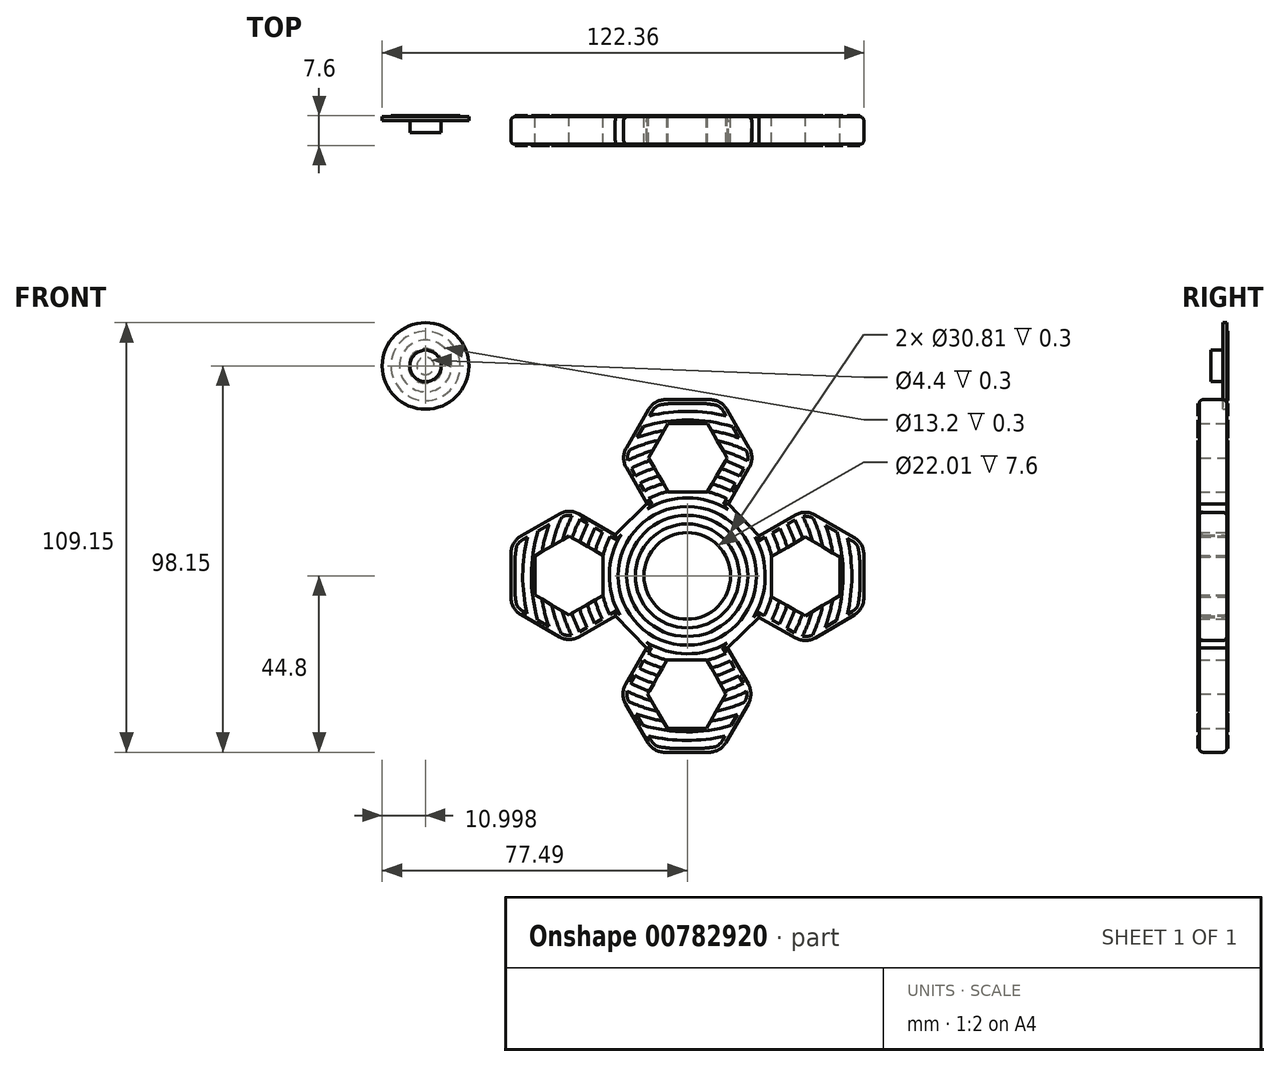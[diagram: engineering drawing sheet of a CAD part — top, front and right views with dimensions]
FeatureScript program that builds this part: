
annotation { "Feature Type Name" : "Feature", "Feature Type Description" : "" }
export const myFeature = defineFeature(function(context is Context, id is Id, definition is map)
    precondition{}
    {
        {
            var Q0;
            Q0=qCreatedBy(makeId("Front.planeOp"),FACE);
            var sketch = newSketch(context, id + "F0", { "sketchPlane" : qUnion([Q0])});
            skCircle(sketch, "E0", {"center": v(0, 0) * mm, "radius": 11 * mm});
            skLineSegment(sketch, "E1.0", {"start": v(-21.35, 5.15) * mm, "end": v(-21.35, -4.88) * mm});
            skLineSegment(sketch, "E1.1", {"start": v(-21.35, -4.88) * mm, "end": v(-30.01, -9.88) * mm});
            skLineSegment(sketch, "E1.2", {"start": v(-30.01, -9.88) * mm, "end": v(-38.67, -4.88) * mm});
            skLineSegment(sketch, "E1.3", {"start": v(-38.67, -4.88) * mm, "end": v(-38.67, 5.12) * mm});
            skLineSegment(sketch, "E1.4", {"start": v(-38.67, 5.12) * mm, "end": v(-30.01, 10.12) * mm});
            skLineSegment(sketch, "E1.5", {"start": v(-30.01, 10.12) * mm, "end": v(-21.35, 5.15) * mm});
            skLineSegment(sketch, "E2.0", {"start": v(10.12, 30.01) * mm, "end": v(5.15, 21.33) * mm});
            skLineSegment(sketch, "E2.1", {"start": v(5.15, 21.33) * mm, "end": v(-4.9, 21.33) * mm});
            skLineSegment(sketch, "E2.2", {"start": v(-4.9, 21.33) * mm, "end": v(-9.89, 30) * mm});
            skLineSegment(sketch, "E2.3", {"start": v(-9.89, 30) * mm, "end": v(-4.88, 38.67) * mm});
            skLineSegment(sketch, "E2.4", {"start": v(-4.88, 38.67) * mm, "end": v(5.12, 38.67) * mm});
            skLineSegment(sketch, "E2.5", {"start": v(5.12, 38.67) * mm, "end": v(10.12, 30.01) * mm});
            skLineSegment(sketch, "E3.0", {"start": v(38.77, -4.96) * mm, "end": v(29.98, -10.14) * mm});
            skLineSegment(sketch, "E3.1", {"start": v(29.98, -10.14) * mm, "end": v(21.45, -5.33) * mm});
            skLineSegment(sketch, "E3.2", {"start": v(21.45, -5.33) * mm, "end": v(21.45, 4.95) * mm});
            skLineSegment(sketch, "E3.3", {"start": v(21.45, 4.95) * mm, "end": v(30, 9.88) * mm});
            skLineSegment(sketch, "E3.4", {"start": v(30, 9.88) * mm, "end": v(38.77, 4.82) * mm});
            skLineSegment(sketch, "E3.5", {"start": v(38.77, 4.82) * mm, "end": v(38.77, -4.96) * mm});
            skLineSegment(sketch, "E4.0", {"start": v(9.88, -30) * mm, "end": v(4.86, -38.7) * mm});
            skLineSegment(sketch, "E4.1", {"start": v(4.86, -38.7) * mm, "end": v(-5.07, -38.7) * mm});
            skLineSegment(sketch, "E4.2", {"start": v(-5.07, -38.7) * mm, "end": v(-10.08, -30.03) * mm});
            skLineSegment(sketch, "E4.3", {"start": v(-10.08, -30.03) * mm, "end": v(-5.1, -21.34) * mm});
            skLineSegment(sketch, "E4.4", {"start": v(-5.1, -21.34) * mm, "end": v(4.9, -21.34) * mm});
            skLineSegment(sketch, "E4.5", {"start": v(4.9, -21.34) * mm, "end": v(9.88, -30) * mm});
            skLineSegment(sketch, "E5.0", {"start": v(-27.52, 15.73) * mm, "end": v(-18.3, 10.44) * mm});
            skLineSegment(sketch, "E5.1", {"start": v(-18.3, -10.17) * mm, "end": v(-27.51, -15.49) * mm});
            skLineSegment(sketch, "E5.2", {"start": v(-32.51, -15.49) * mm, "end": v(-42.28, -9.85) * mm});
            skLineSegment(sketch, "E5.3", {"start": v(-44.78, -5.52) * mm, "end": v(-44.78, 5.76) * mm});
            skLineSegment(sketch, "E5.4", {"start": v(-42.28, 10.09) * mm, "end": v(-32.51, 15.72) * mm});
            skLineSegment(sketch, "E6.0", {"start": v(15.73, 27.52) * mm, "end": v(10.41, 18.25) * mm});
            skLineSegment(sketch, "E6.1", {"start": v(-10.2, 18.34) * mm, "end": v(-15.5, 27.51) * mm});
            skLineSegment(sketch, "E6.2", {"start": v(-15.49, 32.5) * mm, "end": v(-9.85, 42.28) * mm});
            skLineSegment(sketch, "E6.3", {"start": v(-5.52, 44.78) * mm, "end": v(5.76, 44.78) * mm});
            skLineSegment(sketch, "E6.4", {"start": v(10.09, 42.28) * mm, "end": v(15.72, 32.51) * mm});
            skLineSegment(sketch, "E7.0", {"start": v(27.53, -15.77) * mm, "end": v(18.22, -10.51) * mm});
            skLineSegment(sketch, "E7.1", {"start": v(18.27, 10.16) * mm, "end": v(27.5, 15.49) * mm});
            skLineSegment(sketch, "E7.2", {"start": v(32.5, 15.49) * mm, "end": v(42.37, 9.78) * mm});
            skLineSegment(sketch, "E7.3", {"start": v(44.87, 5.45) * mm, "end": v(44.87, -5.59) * mm});
            skLineSegment(sketch, "E7.4", {"start": v(42.41, -9.9) * mm, "end": v(32.53, -15.72) * mm});
            skLineSegment(sketch, "E8.0", {"start": v(-15.69, -27.54) * mm, "end": v(-10.39, -18.3) * mm});
            skLineSegment(sketch, "E8.1", {"start": v(10.21, -18.33) * mm, "end": v(15.49, -27.5) * mm});
            skLineSegment(sketch, "E8.2", {"start": v(15.49, -32.49) * mm, "end": v(9.83, -42.3) * mm});
            skLineSegment(sketch, "E8.3", {"start": v(5.5, -44.8) * mm, "end": v(-5.7, -44.8) * mm});
            skLineSegment(sketch, "E8.4", {"start": v(-10.04, -42.3) * mm, "end": v(-15.68, -32.53) * mm});
            skLineSegment(sketch, "E9", {"start": v(-18.3, -10.17) * mm, "end": v(-10.39, -18.3) * mm});
            skLineSegment(sketch, "E10", {"start": v(10.21, -18.33) * mm, "end": v(18.22, -10.51) * mm});
            skLineSegment(sketch, "E11", {"start": v(18.27, 10.16) * mm, "end": v(10.41, 18.25) * mm});
            skLineSegment(sketch, "E12", {"start": v(-18.3, 10.44) * mm, "end": v(-10.2, 18.34) * mm});
            skPoint(sketch, "E13", {"position": v(-30, 0) * mm});
            skPoint(sketch, "E14", {"position": v(0, 30) * mm});
            skPoint(sketch, "E15", {"position": v(30, 0) * mm});
            skPoint(sketch, "E15.positionSnap0", {"position": v(30, -0.01) * mm});
            skPoint(sketch, "E16", {"position": v(0, -30) * mm});
            skPoint(sketch, "E17.visualSharp", {"position": v(-8.4, 44.78) * mm});
            skArc(sketch, "E17.filletArc", {"start": v(-5.52, 44.78) * mm, "mid": v(-8.02, 44.1) * mm, "end": v(-9.85, 42.28) * mm});
            skPoint(sketch, "E18.visualSharp", {"position": v(8.64, 44.78) * mm});
            skArc(sketch, "E18.filletArc", {"start": v(10.09, 42.28) * mm, "mid": v(8.26, 44.1) * mm, "end": v(5.76, 44.78) * mm});
            skPoint(sketch, "E19.visualSharp", {"position": v(17.16, 30.02) * mm});
            skArc(sketch, "E19.filletArc", {"start": v(15.73, 27.52) * mm, "mid": v(16.4, 30.02) * mm, "end": v(15.72, 32.51) * mm});
            skPoint(sketch, "E20.visualSharp", {"position": v(-16.93, 30.01) * mm});
            skArc(sketch, "E20.filletArc", {"start": v(-15.49, 32.5) * mm, "mid": v(-16.16, 30) * mm, "end": v(-15.5, 27.51) * mm});
            skPoint(sketch, "E21.visualSharp", {"position": v(-30.02, 17.16) * mm});
            skArc(sketch, "E21.filletArc", {"start": v(-27.52, 15.73) * mm, "mid": v(-30.02, 16.4) * mm, "end": v(-32.51, 15.72) * mm});
            skPoint(sketch, "E22.visualSharp", {"position": v(-44.78, 8.64) * mm});
            skArc(sketch, "E22.filletArc", {"start": v(-42.28, 10.09) * mm, "mid": v(-44.1, 8.26) * mm, "end": v(-44.78, 5.76) * mm});
            skPoint(sketch, "E23.visualSharp", {"position": v(-44.78, -8.4) * mm});
            skArc(sketch, "E23.filletArc", {"start": v(-44.78, -5.52) * mm, "mid": v(-44.1, -8.02) * mm, "end": v(-42.28, -9.85) * mm});
            skPoint(sketch, "E24.visualSharp", {"position": v(-30.01, -16.93) * mm});
            skArc(sketch, "E24.filletArc", {"start": v(-32.51, -15.49) * mm, "mid": v(-30.01, -16.16) * mm, "end": v(-27.51, -15.49) * mm});
            skPoint(sketch, "E25.visualSharp", {"position": v(-17.12, -30.04) * mm});
            skArc(sketch, "E25.filletArc", {"start": v(-15.69, -27.54) * mm, "mid": v(-16.35, -30.04) * mm, "end": v(-15.68, -32.53) * mm});
            skPoint(sketch, "E26.visualSharp", {"position": v(-8.6, -44.8) * mm});
            skArc(sketch, "E26.filletArc", {"start": v(-10.04, -42.3) * mm, "mid": v(-8.2, -44.13) * mm, "end": v(-5.7, -44.8) * mm});
            skPoint(sketch, "E27.visualSharp", {"position": v(8.4, -44.8) * mm});
            skArc(sketch, "E27.filletArc", {"start": v(5.5, -44.8) * mm, "mid": v(8, -44.13) * mm, "end": v(9.83, -42.3) * mm});
            skPoint(sketch, "E28.visualSharp", {"position": v(16.93, -30) * mm});
            skArc(sketch, "E28.filletArc", {"start": v(15.49, -32.49) * mm, "mid": v(16.16, -30) * mm, "end": v(15.49, -27.5) * mm});
            skPoint(sketch, "E29.visualSharp", {"position": v(30.04, -17.19) * mm});
            skArc(sketch, "E29.filletArc", {"start": v(27.53, -15.77) * mm, "mid": v(30.04, -16.41) * mm, "end": v(32.53, -15.72) * mm});
            skPoint(sketch, "E30.visualSharp", {"position": v(44.87, -8.44) * mm});
            skArc(sketch, "E30.filletArc", {"start": v(42.41, -9.9) * mm, "mid": v(44.21, -8.07) * mm, "end": v(44.87, -5.59) * mm});
            skPoint(sketch, "E31.visualSharp", {"position": v(44.87, 8.34) * mm});
            skArc(sketch, "E31.filletArc", {"start": v(44.87, 5.45) * mm, "mid": v(44.2, 7.95) * mm, "end": v(42.37, 9.78) * mm});
            skPoint(sketch, "E32.visualSharp", {"position": v(30, 16.93) * mm});
            skArc(sketch, "E32.filletArc", {"start": v(32.5, 15.49) * mm, "mid": v(30, 16.16) * mm, "end": v(27.5, 15.49) * mm});
            skCircle(sketch, "E33", {"center": v(-66.5, 53.35) * mm, "radius": 11 * mm});
            skSolve(sketch);
        }
        {
            var Q0;
            Q0=makeQuery(id+"F0.imprint","IMPRINT",FACE,{"disambiguationData":[TD([[makeQuery(id+"F0.imprint","IMPRINT",EDGE,{"derivedFrom":sQuery(id+"F0.wireOp",EDGE,"E0")}),-1.0]])]});
            extrude(context, id + "F1", {"entities" : qUnion([Q0]), "depth" : 7 * mm, "offsetDistance" : 25 * mm});
        }
        {
            var Q0;
            Q0=makeQuery(id+"F1.opExtrude","CAP_EDGE",EDGE,{"disambiguationData":[OSD([sQuery(id+"F0.wireOp",EDGE,"E8.2")])],"isStart":false});
            var Q1;
            Q1=makeQuery(id+"F1.opExtrude","CAP_EDGE",EDGE,{"disambiguationData":[OSD([sQuery(id+"F0.wireOp",EDGE,"E5.3")])],"isStart":false});
            var Q2;
            Q2=makeQuery(id+"F1.opExtrude","CAP_EDGE",EDGE,{"disambiguationData":[OSD([sQuery(id+"F0.wireOp",EDGE,"E6.2")])],"isStart":false});
            var Q3;
            Q3=makeQuery(id+"F1.opExtrude","CAP_EDGE",EDGE,{"disambiguationData":[OSD([sQuery(id+"F0.wireOp",EDGE,"E7.1")])],"isStart":false});
            var Q4;
            Q4=makeQuery(id+"F1.opExtrude","CAP_EDGE",EDGE,{"disambiguationData":[OSD([sQuery(id+"F0.wireOp",EDGE,"E11")])],"isStart":false});
            var Q5;
            Q5=makeQuery(id+"F1.opExtrude","CAP_EDGE",EDGE,{"disambiguationData":[OSD([sQuery(id+"F0.wireOp",EDGE,"E11")])],"isStart":true});
            var Q6;
            Q6=makeQuery(id+"F1.opExtrude","CAP_EDGE",EDGE,{"disambiguationData":[OSD([sQuery(id+"F0.wireOp",EDGE,"E6.0")])],"isStart":true});
            var Q7;
            Q7=makeQuery(id+"F1.opExtrude","CAP_EDGE",EDGE,{"disambiguationData":[OSD([sQuery(id+"F0.wireOp",EDGE,"E7.2")])],"isStart":true});
            var Q8;
            Q8=makeQuery(id+"F1.opExtrude","CAP_EDGE",EDGE,{"disambiguationData":[OSD([sQuery(id+"F0.wireOp",EDGE,"E12")])],"isStart":true});
            var Q9;
            Q9=makeQuery(id+"F1.opExtrude","CAP_EDGE",EDGE,{"disambiguationData":[OSD([sQuery(id+"F0.wireOp",EDGE,"E5.0")])],"isStart":true});
            var Q10;
            Q10=makeQuery(id+"F1.opExtrude","CAP_EDGE",EDGE,{"disambiguationData":[OSD([sQuery(id+"F0.wireOp",EDGE,"E9")])],"isStart":true});
            var Q11;
            Q11=makeQuery(id+"F1.opExtrude","CAP_EDGE",EDGE,{"disambiguationData":[OSD([sQuery(id+"F0.wireOp",EDGE,"E8.0")])],"isStart":true});
            var Q12;
            Q12=makeQuery(id+"F1.opExtrude","CAP_EDGE",EDGE,{"disambiguationData":[OSD([sQuery(id+"F0.wireOp",EDGE,"E10")])],"isStart":true});
            var Q13;
            Q13=makeQuery(id+"F1.opExtrude","CAP_EDGE",EDGE,{"disambiguationData":[OSD([sQuery(id+"F0.wireOp",EDGE,"E10")])],"isStart":false});
            var Q14;
            Q14=makeQuery(id+"F1.opExtrude","CAP_EDGE",EDGE,{"disambiguationData":[OSD([sQuery(id+"F0.wireOp",EDGE,"E9")])],"isStart":false});
            var Q15;
            Q15=makeQuery(id+"F1.opExtrude","CAP_EDGE",EDGE,{"disambiguationData":[OSD([sQuery(id+"F0.wireOp",EDGE,"E12")])],"isStart":false});
            fillet(context, id + "F2", {"entities" : qUnion([Q0, Q1, Q2, Q3, Q4, Q5, Q6, Q7, Q8, Q9, Q10, Q11, Q12, Q13, Q14, Q15]), "radius" : 1 * mm, "tangentPropagation" : true, "allowEdgeOverflow" : false});
        }
        {
            var Q0;
            Q0=makeQuery(id+"F1.opExtrude","CAP_FACE",FACE,{"disambiguationData":[OSD([sQuery(id+"F0.wireOp",EDGE,"E0"),sQuery(id+"F0.wireOp",EDGE,"E1.0"),sQuery(id+"F0.wireOp",EDGE,"E1.1"),sQuery(id+"F0.wireOp",EDGE,"E1.2"),sQuery(id+"F0.wireOp",EDGE,"E1.3"),sQuery(id+"F0.wireOp",EDGE,"E1.4"),sQuery(id+"F0.wireOp",EDGE,"E1.5"),sQuery(id+"F0.wireOp",EDGE,"E2.0"),sQuery(id+"F0.wireOp",EDGE,"E2.1"),sQuery(id+"F0.wireOp",EDGE,"E2.2"),sQuery(id+"F0.wireOp",EDGE,"E2.3"),sQuery(id+"F0.wireOp",EDGE,"E2.4"),sQuery(id+"F0.wireOp",EDGE,"E2.5"),sQuery(id+"F0.wireOp",EDGE,"E3.0"),sQuery(id+"F0.wireOp",EDGE,"E3.1"),sQuery(id+"F0.wireOp",EDGE,"E3.2"),sQuery(id+"F0.wireOp",EDGE,"E3.3"),sQuery(id+"F0.wireOp",EDGE,"E3.4"),sQuery(id+"F0.wireOp",EDGE,"E3.5"),sQuery(id+"F0.wireOp",EDGE,"E4.0"),sQuery(id+"F0.wireOp",EDGE,"E4.1"),sQuery(id+"F0.wireOp",EDGE,"E4.2"),sQuery(id+"F0.wireOp",EDGE,"E4.3"),sQuery(id+"F0.wireOp",EDGE,"E4.4"),sQuery(id+"F0.wireOp",EDGE,"E4.5"),sQuery(id+"F0.wireOp",EDGE,"E5.0"),sQuery(id+"F0.wireOp",EDGE,"E5.1"),sQuery(id+"F0.wireOp",EDGE,"E5.2"),sQuery(id+"F0.wireOp",EDGE,"E5.3"),sQuery(id+"F0.wireOp",EDGE,"E5.4"),sQuery(id+"F0.wireOp",EDGE,"E6.0"),sQuery(id+"F0.wireOp",EDGE,"E6.1"),sQuery(id+"F0.wireOp",EDGE,"E6.2"),sQuery(id+"F0.wireOp",EDGE,"E6.3"),sQuery(id+"F0.wireOp",EDGE,"E6.4"),sQuery(id+"F0.wireOp",EDGE,"E7.0"),sQuery(id+"F0.wireOp",EDGE,"E7.1"),sQuery(id+"F0.wireOp",EDGE,"E7.2"),sQuery(id+"F0.wireOp",EDGE,"E7.3"),sQuery(id+"F0.wireOp",EDGE,"E7.4"),sQuery(id+"F0.wireOp",EDGE,"E8.0"),sQuery(id+"F0.wireOp",EDGE,"E8.1"),sQuery(id+"F0.wireOp",EDGE,"E8.2"),sQuery(id+"F0.wireOp",EDGE,"E8.3"),sQuery(id+"F0.wireOp",EDGE,"E8.4"),sQuery(id+"F0.wireOp",EDGE,"E9"),sQuery(id+"F0.wireOp",EDGE,"E10"),sQuery(id+"F0.wireOp",EDGE,"E11"),sQuery(id+"F0.wireOp",EDGE,"E12"),sQuery(id+"F0.wireOp",EDGE,"E17.filletArc"),sQuery(id+"F0.wireOp",EDGE,"E18.filletArc"),sQuery(id+"F0.wireOp",EDGE,"E19.filletArc"),sQuery(id+"F0.wireOp",EDGE,"E20.filletArc"),sQuery(id+"F0.wireOp",EDGE,"E21.filletArc"),sQuery(id+"F0.wireOp",EDGE,"E22.filletArc"),sQuery(id+"F0.wireOp",EDGE,"E23.filletArc"),sQuery(id+"F0.wireOp",EDGE,"E24.filletArc"),sQuery(id+"F0.wireOp",EDGE,"E25.filletArc"),sQuery(id+"F0.wireOp",EDGE,"E26.filletArc"),sQuery(id+"F0.wireOp",EDGE,"E27.filletArc"),sQuery(id+"F0.wireOp",EDGE,"E28.filletArc"),sQuery(id+"F0.wireOp",EDGE,"E29.filletArc"),sQuery(id+"F0.wireOp",EDGE,"E30.filletArc"),sQuery(id+"F0.wireOp",EDGE,"E31.filletArc"),sQuery(id+"F0.wireOp",EDGE,"E32.filletArc")])],"isStart":false});
            var sketch = newSketch(context, id + "F3", { "sketchPlane" : qUnion([Q0])});
            skLineSegment(sketch, "E34", {"start": v(0, -2.4) * mm, "end": v(0, -77.28) * mm});
            skLineSegment(sketch, "E35", {"start": v(0, -2.4) * mm, "end": v(0, 53.22) * mm});
            skLineSegment(sketch, "E36", {"start": v(0, 0) * mm, "end": v(-74.78, 0) * mm});
            skLineSegment(sketch, "E37", {"start": v(0, 0) * mm, "end": v(76.06, 0) * mm});
            skCircle(sketch, "E38.0", {"center": v(0, 0) * mm, "radius": 13.2 * mm});
            skCircle(sketch, "E39.0", {"center": v(0, 0) * mm, "radius": 15.4 * mm});
            skCircle(sketch, "E40.0", {"center": v(0, 0) * mm, "radius": 17.6 * mm});
            skCircle(sketch, "E41.0", {"center": v(0, 0) * mm, "radius": 19.8 * mm});
            skCircle(sketch, "E42.0", {"center": v(0, 0) * mm, "radius": 22 * mm});
            skCircle(sketch, "E43.0", {"center": v(0, 0) * mm, "radius": 24.2 * mm});
            skCircle(sketch, "E44.0", {"center": v(0, 0) * mm, "radius": 26.4 * mm});
            skCircle(sketch, "E45.0", {"center": v(0, 0) * mm, "radius": 28.6 * mm});
            skCircle(sketch, "E46.0", {"center": v(0, 0) * mm, "radius": 30.8 * mm});
            skCircle(sketch, "E47.0", {"center": v(0, 0) * mm, "radius": 33 * mm});
            skCircle(sketch, "E48.0", {"center": v(0, 0) * mm, "radius": 35.2 * mm});
            skCircle(sketch, "E49.0", {"center": v(0, 0) * mm, "radius": 37.4 * mm});
            skCircle(sketch, "E50.0", {"center": v(0, 0) * mm, "radius": 39.6 * mm});
            skCircle(sketch, "E51.0", {"center": v(0, 0) * mm, "radius": 41.8 * mm});
            skCircle(sketch, "E52.0", {"center": v(0, 0) * mm, "radius": 44 * mm});
            skSolve(sketch);
        }
        {
            var Q0;
            {var subQ9=sQuery(id+"F3.wireOp",EDGE,"E51.0");var subQ10=sQuery(id+"F3.wireOp",EDGE,"E35");var subQ11=makeQuery(id+"F3.imprint","INTERSECT",VERTEX,{"derivedFrom":[subQ10,subQ9]});Q0=makeQuery(id+"F3.imprint","IMPRINT",FACE,{"disambiguationData":[TD([[makeQuery(id+"F3.imprint","IMPRINT",EDGE,{"disambiguationData":[TD([[subQ11,-1.0]])],"derivedFrom":subQ10}),1.0]])]});}
            var Q1;
            {var subQ7=sQuery(id+"F3.wireOp",EDGE,"E51.0");var subQ13=sQuery(id+"F3.wireOp",EDGE,"E35");var subQ15=makeQuery(id+"F3.imprint","INTERSECT",VERTEX,{"derivedFrom":[subQ13,subQ7]});Q1=makeQuery(id+"F3.imprint","IMPRINT",FACE,{"disambiguationData":[TD([[makeQuery(id+"F3.imprint","IMPRINT",EDGE,{"disambiguationData":[TD([[subQ15,-1.0]])],"derivedFrom":subQ13}),-1.0]])]});}
            var Q2;
            {var subQ10=sQuery(id+"F3.wireOp",EDGE,"E50.0");var subQ11=sQuery(id+"F3.wireOp",EDGE,"E35");var subQ12=makeQuery(id+"F3.imprint","INTERSECT",VERTEX,{"derivedFrom":[subQ11,subQ10]});Q2=makeQuery(id+"F3.imprint","IMPRINT",FACE,{"disambiguationData":[TD([[makeQuery(id+"F3.imprint","IMPRINT",EDGE,{"disambiguationData":[TD([[subQ12,1.0]])],"derivedFrom":subQ11}),1.0]])]});}
            var Q3;
            {var subQ5=sQuery(id+"F3.wireOp",EDGE,"E35");var subQ7=sQuery(id+"F3.wireOp",EDGE,"E50.0");var subQ8=makeQuery(id+"F3.imprint","INTERSECT",VERTEX,{"derivedFrom":[subQ5,subQ7]});Q3=makeQuery(id+"F3.imprint","IMPRINT",FACE,{"disambiguationData":[TD([[makeQuery(id+"F3.imprint","IMPRINT",EDGE,{"disambiguationData":[TD([[subQ8,1.0]])],"derivedFrom":subQ5}),-1.0]])]});}
            var Q4;
            {var subQ2=sQuery(id+"F0.wireOp",EDGE,"E2.3");var subQ7=sQuery(id+"F3.wireOp",EDGE,"E47.0");var subQ11=makeQuery(id+"F1.opExtrude","CAP_EDGE",EDGE,{"disambiguationData":[OSD([subQ2])],"isStart":false});var subQ13=makeQuery(id+"F3.imprint","INTERSECT",VERTEX,{"derivedFrom":[subQ11,subQ7]});Q4=makeQuery(id+"F3.imprint","IMPRINT",FACE,{"disambiguationData":[TD([[makeQuery(id+"F3.imprint","IMPRINT",EDGE,{"disambiguationData":[TD([[subQ13,-1.0]])],"derivedFrom":subQ11}),1.0]])]});}
            var Q5;
            {var subQ0=sQuery(id+"F3.wireOp",EDGE,"E47.0");var subQ2=sQuery(id+"F0.wireOp",EDGE,"E2.5");var subQ5=makeQuery(id+"F1.opExtrude","CAP_EDGE",EDGE,{"disambiguationData":[OSD([subQ2])],"isStart":false});var subQ6=makeQuery(id+"F3.imprint","INTERSECT",VERTEX,{"derivedFrom":[subQ5,subQ0]});Q5=makeQuery(id+"F3.imprint","IMPRINT",FACE,{"disambiguationData":[TD([[makeQuery(id+"F3.imprint","IMPRINT",EDGE,{"disambiguationData":[TD([[subQ6,1.0]])],"derivedFrom":subQ5}),1.0]])]});}
            var Q6;
            {var subQ0=sQuery(id+"F3.wireOp",EDGE,"E45.0");var subQ1=sQuery(id+"F0.wireOp",EDGE,"E2.2");var subQ2=makeQuery(id+"F1.opExtrude","CAP_EDGE",EDGE,{"disambiguationData":[OSD([subQ1])],"isStart":false});var subQ3=makeQuery(id+"F3.imprint","INTERSECT",VERTEX,{"derivedFrom":[subQ2,subQ0]});Q6=makeQuery(id+"F3.imprint","IMPRINT",FACE,{"disambiguationData":[TD([[makeQuery(id+"F3.imprint","IMPRINT",EDGE,{"disambiguationData":[TD([[subQ3,-1.0]])],"derivedFrom":subQ2}),1.0]])]});}
            var Q7;
            {var subQ0=sQuery(id+"F3.wireOp",EDGE,"E45.0");var subQ2=sQuery(id+"F0.wireOp",EDGE,"E2.0");var subQ5=makeQuery(id+"F1.opExtrude","CAP_EDGE",EDGE,{"disambiguationData":[OSD([subQ2])],"isStart":false});var subQ6=makeQuery(id+"F3.imprint","INTERSECT",VERTEX,{"derivedFrom":[subQ5,subQ0]});Q7=makeQuery(id+"F3.imprint","IMPRINT",FACE,{"disambiguationData":[TD([[makeQuery(id+"F3.imprint","IMPRINT",EDGE,{"disambiguationData":[TD([[subQ6,1.0]])],"derivedFrom":subQ5}),1.0]])]});}
            var Q8;
            {var subQ0=sQuery(id+"F3.wireOp",EDGE,"E43.0");var subQ1=sQuery(id+"F0.wireOp",EDGE,"E2.2");var subQ2=makeQuery(id+"F1.opExtrude","CAP_EDGE",EDGE,{"disambiguationData":[OSD([subQ1])],"isStart":false});var subQ3=makeQuery(id+"F3.imprint","INTERSECT",VERTEX,{"derivedFrom":[subQ2,subQ0]});Q8=makeQuery(id+"F3.imprint","IMPRINT",FACE,{"disambiguationData":[TD([[makeQuery(id+"F3.imprint","IMPRINT",EDGE,{"disambiguationData":[TD([[subQ3,-1.0]])],"derivedFrom":subQ2}),1.0]])]});}
            var Q9;
            {var subQ0=sQuery(id+"F3.wireOp",EDGE,"E43.0");var subQ2=sQuery(id+"F0.wireOp",EDGE,"E2.0");var subQ5=makeQuery(id+"F1.opExtrude","CAP_EDGE",EDGE,{"disambiguationData":[OSD([subQ2])],"isStart":false});var subQ6=makeQuery(id+"F3.imprint","INTERSECT",VERTEX,{"derivedFrom":[subQ5,subQ0]});Q9=makeQuery(id+"F3.imprint","IMPRINT",FACE,{"disambiguationData":[TD([[makeQuery(id+"F3.imprint","IMPRINT",EDGE,{"disambiguationData":[TD([[subQ6,1.0]])],"derivedFrom":subQ5}),1.0]])]});}
            var Q10;
            {var subQ10=sQuery(id+"F3.wireOp",EDGE,"E41.0");var subQ11=sQuery(id+"F3.wireOp",EDGE,"E35");var subQ12=makeQuery(id+"F3.imprint","INTERSECT",VERTEX,{"derivedFrom":[subQ11,subQ10]});Q10=makeQuery(id+"F3.imprint","IMPRINT",FACE,{"disambiguationData":[TD([[makeQuery(id+"F3.imprint","IMPRINT",EDGE,{"disambiguationData":[TD([[subQ12,-1.0]])],"derivedFrom":subQ11}),1.0]])]});}
            var Q11;
            {var subQ12=sQuery(id+"F3.wireOp",EDGE,"E41.0");var subQ13=sQuery(id+"F3.wireOp",EDGE,"E35");var subQ14=makeQuery(id+"F3.imprint","INTERSECT",VERTEX,{"derivedFrom":[subQ13,subQ12]});Q11=makeQuery(id+"F3.imprint","IMPRINT",FACE,{"disambiguationData":[TD([[makeQuery(id+"F3.imprint","IMPRINT",EDGE,{"disambiguationData":[TD([[subQ14,-1.0]])],"derivedFrom":subQ13}),-1.0]])]});}
            var Q12;
            {var subQ0=sQuery(id+"F3.wireOp",EDGE,"E39.0");var subQ1=sQuery(id+"F3.wireOp",EDGE,"E35");var subQ2=makeQuery(id+"F3.imprint","INTERSECT",VERTEX,{"derivedFrom":[subQ1,subQ0]});Q12=makeQuery(id+"F3.imprint","IMPRINT",FACE,{"disambiguationData":[TD([[makeQuery(id+"F3.imprint","IMPRINT",EDGE,{"disambiguationData":[TD([[subQ2,-1.0]])],"derivedFrom":subQ1}),1.0]])]});}
            var Q13;
            {var subQ0=sQuery(id+"F3.wireOp",EDGE,"E39.0");var subQ1=sQuery(id+"F3.wireOp",EDGE,"E35");var subQ2=makeQuery(id+"F3.imprint","INTERSECT",VERTEX,{"derivedFrom":[subQ1,subQ0]});Q13=makeQuery(id+"F3.imprint","IMPRINT",FACE,{"disambiguationData":[TD([[makeQuery(id+"F3.imprint","IMPRINT",EDGE,{"disambiguationData":[TD([[subQ2,-1.0]])],"derivedFrom":subQ1}),-1.0]])]});}
            var Q14;
            {var subQ0=sQuery(id+"F3.wireOp",EDGE,"E38.0");var subQ1=sQuery(id+"F3.wireOp",EDGE,"E35");var subQ2=makeQuery(id+"F3.imprint","INTERSECT",VERTEX,{"derivedFrom":[subQ1,subQ0]});Q14=makeQuery(id+"F3.imprint","IMPRINT",FACE,{"disambiguationData":[TD([[makeQuery(id+"F3.imprint","IMPRINT",EDGE,{"disambiguationData":[TD([[subQ2,1.0]])],"derivedFrom":subQ1}),1.0]])]});}
            var Q15;
            {var subQ0=sQuery(id+"F3.wireOp",EDGE,"E38.0");var subQ1=sQuery(id+"F3.wireOp",EDGE,"E35");var subQ2=makeQuery(id+"F3.imprint","INTERSECT",VERTEX,{"derivedFrom":[subQ1,subQ0]});Q15=makeQuery(id+"F3.imprint","IMPRINT",FACE,{"disambiguationData":[TD([[makeQuery(id+"F3.imprint","IMPRINT",EDGE,{"disambiguationData":[TD([[subQ2,1.0]])],"derivedFrom":subQ1}),-1.0]])]});}
            var Q16;
            {var subQ9=sQuery(id+"F3.wireOp",EDGE,"E41.0");var subQ10=sQuery(id+"F3.wireOp",EDGE,"E37");var subQ11=makeQuery(id+"F3.imprint","INTERSECT",VERTEX,{"derivedFrom":[subQ10,subQ9]});Q16=makeQuery(id+"F3.imprint","IMPRINT",FACE,{"disambiguationData":[TD([[makeQuery(id+"F3.imprint","IMPRINT",EDGE,{"disambiguationData":[TD([[subQ11,-1.0]])],"derivedFrom":subQ10}),1.0]])]});}
            var Q17;
            {var subQ0=sQuery(id+"F3.wireOp",EDGE,"E43.0");var subQ1=sQuery(id+"F0.wireOp",EDGE,"E3.3");var subQ2=makeQuery(id+"F1.opExtrude","CAP_EDGE",EDGE,{"disambiguationData":[OSD([subQ1])],"isStart":false});var subQ3=makeQuery(id+"F3.imprint","INTERSECT",VERTEX,{"derivedFrom":[subQ2,subQ0]});Q17=makeQuery(id+"F3.imprint","IMPRINT",FACE,{"disambiguationData":[TD([[makeQuery(id+"F3.imprint","IMPRINT",EDGE,{"disambiguationData":[TD([[subQ3,-1.0]])],"derivedFrom":subQ2}),1.0]])]});}
            var Q18;
            {var subQ0=sQuery(id+"F3.wireOp",EDGE,"E45.0");var subQ1=sQuery(id+"F0.wireOp",EDGE,"E3.3");var subQ2=makeQuery(id+"F1.opExtrude","CAP_EDGE",EDGE,{"disambiguationData":[OSD([subQ1])],"isStart":false});var subQ3=makeQuery(id+"F3.imprint","INTERSECT",VERTEX,{"derivedFrom":[subQ2,subQ0]});Q18=makeQuery(id+"F3.imprint","IMPRINT",FACE,{"disambiguationData":[TD([[makeQuery(id+"F3.imprint","IMPRINT",EDGE,{"disambiguationData":[TD([[subQ3,-1.0]])],"derivedFrom":subQ2}),1.0]])]});}
            var Q19;
            {var subQ2=sQuery(id+"F0.wireOp",EDGE,"E3.4");var subQ7=sQuery(id+"F3.wireOp",EDGE,"E47.0");var subQ11=makeQuery(id+"F1.opExtrude","CAP_EDGE",EDGE,{"disambiguationData":[OSD([subQ2])],"isStart":false});var subQ12=makeQuery(id+"F3.imprint","INTERSECT",VERTEX,{"derivedFrom":[subQ11,subQ7]});Q19=makeQuery(id+"F3.imprint","IMPRINT",FACE,{"disambiguationData":[TD([[makeQuery(id+"F3.imprint","IMPRINT",EDGE,{"disambiguationData":[TD([[subQ12,-1.0]])],"derivedFrom":subQ11}),1.0]])]});}
            var Q20;
            {var subQ0=sQuery(id+"F3.wireOp",EDGE,"E50.0");var subQ1=sQuery(id+"F3.wireOp",EDGE,"E37");var subQ2=makeQuery(id+"F3.imprint","INTERSECT",VERTEX,{"derivedFrom":[subQ1,subQ0]});Q20=makeQuery(id+"F3.imprint","IMPRINT",FACE,{"disambiguationData":[TD([[makeQuery(id+"F3.imprint","IMPRINT",EDGE,{"disambiguationData":[TD([[subQ2,1.0]])],"derivedFrom":subQ1}),1.0]])]});}
            var Q21;
            {var subQ7=sQuery(id+"F3.wireOp",EDGE,"E51.0");var subQ13=sQuery(id+"F3.wireOp",EDGE,"E37");var subQ14=makeQuery(id+"F3.imprint","INTERSECT",VERTEX,{"derivedFrom":[subQ13,subQ7]});Q21=makeQuery(id+"F3.imprint","IMPRINT",FACE,{"disambiguationData":[TD([[makeQuery(id+"F3.imprint","IMPRINT",EDGE,{"disambiguationData":[TD([[subQ14,-1.0]])],"derivedFrom":subQ13}),1.0]])]});}
            var Q22;
            {var subQ7=sQuery(id+"F3.wireOp",EDGE,"E51.0");var subQ13=sQuery(id+"F3.wireOp",EDGE,"E37");var subQ14=makeQuery(id+"F3.imprint","INTERSECT",VERTEX,{"derivedFrom":[subQ13,subQ7]});Q22=makeQuery(id+"F3.imprint","IMPRINT",FACE,{"disambiguationData":[TD([[makeQuery(id+"F3.imprint","IMPRINT",EDGE,{"disambiguationData":[TD([[subQ14,-1.0]])],"derivedFrom":subQ13}),-1.0]])]});}
            var Q23;
            {var subQ0=sQuery(id+"F3.wireOp",EDGE,"E50.0");var subQ1=sQuery(id+"F3.wireOp",EDGE,"E37");var subQ2=makeQuery(id+"F3.imprint","INTERSECT",VERTEX,{"derivedFrom":[subQ1,subQ0]});Q23=makeQuery(id+"F3.imprint","IMPRINT",FACE,{"disambiguationData":[TD([[makeQuery(id+"F3.imprint","IMPRINT",EDGE,{"disambiguationData":[TD([[subQ2,1.0]])],"derivedFrom":subQ1}),-1.0]])]});}
            var Q24;
            {var subQ0=sQuery(id+"F3.wireOp",EDGE,"E47.0");var subQ2=sQuery(id+"F0.wireOp",EDGE,"E3.0");var subQ5=makeQuery(id+"F1.opExtrude","CAP_EDGE",EDGE,{"disambiguationData":[OSD([subQ2])],"isStart":false});var subQ6=makeQuery(id+"F3.imprint","INTERSECT",VERTEX,{"derivedFrom":[subQ5,subQ0]});Q24=makeQuery(id+"F3.imprint","IMPRINT",FACE,{"disambiguationData":[TD([[makeQuery(id+"F3.imprint","IMPRINT",EDGE,{"disambiguationData":[TD([[subQ6,1.0]])],"derivedFrom":subQ5}),1.0]])]});}
            var Q25;
            {var subQ0=sQuery(id+"F3.wireOp",EDGE,"E45.0");var subQ2=sQuery(id+"F0.wireOp",EDGE,"E3.1");var subQ5=makeQuery(id+"F1.opExtrude","CAP_EDGE",EDGE,{"disambiguationData":[OSD([subQ2])],"isStart":false});var subQ6=makeQuery(id+"F3.imprint","INTERSECT",VERTEX,{"derivedFrom":[subQ5,subQ0]});Q25=makeQuery(id+"F3.imprint","IMPRINT",FACE,{"disambiguationData":[TD([[makeQuery(id+"F3.imprint","IMPRINT",EDGE,{"disambiguationData":[TD([[subQ6,1.0]])],"derivedFrom":subQ5}),1.0]])]});}
            var Q26;
            {var subQ0=sQuery(id+"F3.wireOp",EDGE,"E43.0");var subQ2=sQuery(id+"F0.wireOp",EDGE,"E3.1");var subQ5=makeQuery(id+"F1.opExtrude","CAP_EDGE",EDGE,{"disambiguationData":[OSD([subQ2])],"isStart":false});var subQ6=makeQuery(id+"F3.imprint","INTERSECT",VERTEX,{"derivedFrom":[subQ5,subQ0]});Q26=makeQuery(id+"F3.imprint","IMPRINT",FACE,{"disambiguationData":[TD([[makeQuery(id+"F3.imprint","IMPRINT",EDGE,{"disambiguationData":[TD([[subQ6,1.0]])],"derivedFrom":subQ5}),1.0]])]});}
            var Q27;
            {var subQ9=sQuery(id+"F3.wireOp",EDGE,"E41.0");var subQ10=sQuery(id+"F3.wireOp",EDGE,"E37");var subQ11=makeQuery(id+"F3.imprint","INTERSECT",VERTEX,{"derivedFrom":[subQ10,subQ9]});Q27=makeQuery(id+"F3.imprint","IMPRINT",FACE,{"disambiguationData":[TD([[makeQuery(id+"F3.imprint","IMPRINT",EDGE,{"disambiguationData":[TD([[subQ11,-1.0]])],"derivedFrom":subQ10}),-1.0]])]});}
            var Q28;
            {var subQ0=sQuery(id+"F3.wireOp",EDGE,"E39.0");var subQ1=sQuery(id+"F3.wireOp",EDGE,"E34");var subQ2=makeQuery(id+"F3.imprint","INTERSECT",VERTEX,{"derivedFrom":[subQ1,subQ0]});Q28=makeQuery(id+"F3.imprint","IMPRINT",FACE,{"disambiguationData":[TD([[makeQuery(id+"F3.imprint","IMPRINT",EDGE,{"disambiguationData":[TD([[subQ2,-1.0]])],"derivedFrom":subQ1}),1.0]])]});}
            var Q29;
            {var subQ0=sQuery(id+"F3.wireOp",EDGE,"E38.0");var subQ1=sQuery(id+"F3.wireOp",EDGE,"E34");var subQ2=makeQuery(id+"F3.imprint","INTERSECT",VERTEX,{"derivedFrom":[subQ1,subQ0]});Q29=makeQuery(id+"F3.imprint","IMPRINT",FACE,{"disambiguationData":[TD([[makeQuery(id+"F3.imprint","IMPRINT",EDGE,{"disambiguationData":[TD([[subQ2,1.0]])],"derivedFrom":subQ1}),1.0]])]});}
            var Q30;
            {var subQ0=sQuery(id+"F3.wireOp",EDGE,"E38.0");var subQ1=sQuery(id+"F3.wireOp",EDGE,"E34");var subQ2=makeQuery(id+"F3.imprint","INTERSECT",VERTEX,{"derivedFrom":[subQ1,subQ0]});Q30=makeQuery(id+"F3.imprint","IMPRINT",FACE,{"disambiguationData":[TD([[makeQuery(id+"F3.imprint","IMPRINT",EDGE,{"disambiguationData":[TD([[subQ2,1.0]])],"derivedFrom":subQ1}),-1.0]])]});}
            var Q31;
            {var subQ0=sQuery(id+"F3.wireOp",EDGE,"E39.0");var subQ1=sQuery(id+"F3.wireOp",EDGE,"E34");var subQ2=makeQuery(id+"F3.imprint","INTERSECT",VERTEX,{"derivedFrom":[subQ1,subQ0]});Q31=makeQuery(id+"F3.imprint","IMPRINT",FACE,{"disambiguationData":[TD([[makeQuery(id+"F3.imprint","IMPRINT",EDGE,{"disambiguationData":[TD([[subQ2,-1.0]])],"derivedFrom":subQ1}),-1.0]])]});}
            var Q32;
            {var subQ5=sQuery(id+"F3.wireOp",EDGE,"E36");var subQ14=sQuery(id+"F3.wireOp",EDGE,"E41.0");var subQ15=makeQuery(id+"F3.imprint","INTERSECT",VERTEX,{"derivedFrom":[subQ5,subQ14]});Q32=makeQuery(id+"F3.imprint","IMPRINT",FACE,{"disambiguationData":[TD([[makeQuery(id+"F3.imprint","IMPRINT",EDGE,{"disambiguationData":[TD([[subQ15,-1.0]])],"derivedFrom":subQ5}),1.0]])]});}
            var Q33;
            {var subQ5=sQuery(id+"F3.wireOp",EDGE,"E36");var subQ14=sQuery(id+"F3.wireOp",EDGE,"E41.0");var subQ15=makeQuery(id+"F3.imprint","INTERSECT",VERTEX,{"derivedFrom":[subQ5,subQ14]});Q33=makeQuery(id+"F3.imprint","IMPRINT",FACE,{"disambiguationData":[TD([[makeQuery(id+"F3.imprint","IMPRINT",EDGE,{"disambiguationData":[TD([[subQ15,-1.0]])],"derivedFrom":subQ5}),-1.0]])]});}
            var Q34;
            {var subQ0=sQuery(id+"F3.wireOp",EDGE,"E43.0");var subQ2=sQuery(id+"F0.wireOp",EDGE,"E1.5");var subQ5=makeQuery(id+"F1.opExtrude","CAP_EDGE",EDGE,{"disambiguationData":[OSD([subQ2])],"isStart":false});var subQ6=makeQuery(id+"F3.imprint","INTERSECT",VERTEX,{"derivedFrom":[subQ5,subQ0]});Q34=makeQuery(id+"F3.imprint","IMPRINT",FACE,{"disambiguationData":[TD([[makeQuery(id+"F3.imprint","IMPRINT",EDGE,{"disambiguationData":[TD([[subQ6,1.0]])],"derivedFrom":subQ5}),1.0]])]});}
            var Q35;
            {var subQ0=sQuery(id+"F3.wireOp",EDGE,"E45.0");var subQ2=sQuery(id+"F0.wireOp",EDGE,"E1.5");var subQ5=makeQuery(id+"F1.opExtrude","CAP_EDGE",EDGE,{"disambiguationData":[OSD([subQ2])],"isStart":false});var subQ6=makeQuery(id+"F3.imprint","INTERSECT",VERTEX,{"derivedFrom":[subQ5,subQ0]});Q35=makeQuery(id+"F3.imprint","IMPRINT",FACE,{"disambiguationData":[TD([[makeQuery(id+"F3.imprint","IMPRINT",EDGE,{"disambiguationData":[TD([[subQ6,1.0]])],"derivedFrom":subQ5}),1.0]])]});}
            var Q36;
            {var subQ0=sQuery(id+"F3.wireOp",EDGE,"E47.0");var subQ2=sQuery(id+"F0.wireOp",EDGE,"E1.4");var subQ5=makeQuery(id+"F1.opExtrude","CAP_EDGE",EDGE,{"disambiguationData":[OSD([subQ2])],"isStart":false});var subQ6=makeQuery(id+"F3.imprint","INTERSECT",VERTEX,{"derivedFrom":[subQ5,subQ0]});Q36=makeQuery(id+"F3.imprint","IMPRINT",FACE,{"disambiguationData":[TD([[makeQuery(id+"F3.imprint","IMPRINT",EDGE,{"disambiguationData":[TD([[subQ6,1.0]])],"derivedFrom":subQ5}),1.0]])]});}
            var Q37;
            {var subQ5=sQuery(id+"F3.wireOp",EDGE,"E36");var subQ7=sQuery(id+"F3.wireOp",EDGE,"E50.0");var subQ8=makeQuery(id+"F3.imprint","INTERSECT",VERTEX,{"derivedFrom":[subQ5,subQ7]});Q37=makeQuery(id+"F3.imprint","IMPRINT",FACE,{"disambiguationData":[TD([[makeQuery(id+"F3.imprint","IMPRINT",EDGE,{"disambiguationData":[TD([[subQ8,1.0]])],"derivedFrom":subQ5}),-1.0]])]});}
            var Q38;
            {var subQ7=sQuery(id+"F3.wireOp",EDGE,"E51.0");var subQ13=sQuery(id+"F3.wireOp",EDGE,"E36");var subQ14=makeQuery(id+"F3.imprint","INTERSECT",VERTEX,{"derivedFrom":[subQ13,subQ7]});Q38=makeQuery(id+"F3.imprint","IMPRINT",FACE,{"disambiguationData":[TD([[makeQuery(id+"F3.imprint","IMPRINT",EDGE,{"disambiguationData":[TD([[subQ14,-1.0]])],"derivedFrom":subQ13}),-1.0]])]});}
            var Q39;
            {var subQ7=sQuery(id+"F3.wireOp",EDGE,"E51.0");var subQ9=sQuery(id+"F3.wireOp",EDGE,"E36");var subQ10=makeQuery(id+"F3.imprint","INTERSECT",VERTEX,{"derivedFrom":[subQ9,subQ7]});Q39=makeQuery(id+"F3.imprint","IMPRINT",FACE,{"disambiguationData":[TD([[makeQuery(id+"F3.imprint","IMPRINT",EDGE,{"disambiguationData":[TD([[subQ10,-1.0]])],"derivedFrom":subQ9}),1.0]])]});}
            var Q40;
            {var subQ7=sQuery(id+"F3.wireOp",EDGE,"E50.0");var subQ8=sQuery(id+"F3.wireOp",EDGE,"E36");var subQ9=makeQuery(id+"F3.imprint","INTERSECT",VERTEX,{"derivedFrom":[subQ8,subQ7]});Q40=makeQuery(id+"F3.imprint","IMPRINT",FACE,{"disambiguationData":[TD([[makeQuery(id+"F3.imprint","IMPRINT",EDGE,{"disambiguationData":[TD([[subQ9,1.0]])],"derivedFrom":subQ8}),1.0]])]});}
            var Q41;
            {var subQ2=sQuery(id+"F0.wireOp",EDGE,"E1.2");var subQ9=sQuery(id+"F3.wireOp",EDGE,"E47.0");var subQ11=makeQuery(id+"F1.opExtrude","CAP_EDGE",EDGE,{"disambiguationData":[OSD([subQ2])],"isStart":false});var subQ13=makeQuery(id+"F3.imprint","INTERSECT",VERTEX,{"derivedFrom":[subQ11,subQ9]});Q41=makeQuery(id+"F3.imprint","IMPRINT",FACE,{"disambiguationData":[TD([[makeQuery(id+"F3.imprint","IMPRINT",EDGE,{"disambiguationData":[TD([[subQ13,-1.0]])],"derivedFrom":subQ11}),1.0]])]});}
            var Q42;
            {var subQ0=sQuery(id+"F3.wireOp",EDGE,"E45.0");var subQ1=sQuery(id+"F0.wireOp",EDGE,"E1.1");var subQ2=makeQuery(id+"F1.opExtrude","CAP_EDGE",EDGE,{"disambiguationData":[OSD([subQ1])],"isStart":false});var subQ3=makeQuery(id+"F3.imprint","INTERSECT",VERTEX,{"derivedFrom":[subQ2,subQ0]});Q42=makeQuery(id+"F3.imprint","IMPRINT",FACE,{"disambiguationData":[TD([[makeQuery(id+"F3.imprint","IMPRINT",EDGE,{"disambiguationData":[TD([[subQ3,-1.0]])],"derivedFrom":subQ2}),1.0]])]});}
            var Q43;
            {var subQ0=sQuery(id+"F3.wireOp",EDGE,"E43.0");var subQ1=sQuery(id+"F0.wireOp",EDGE,"E1.1");var subQ2=makeQuery(id+"F1.opExtrude","CAP_EDGE",EDGE,{"disambiguationData":[OSD([subQ1])],"isStart":false});var subQ3=makeQuery(id+"F3.imprint","INTERSECT",VERTEX,{"derivedFrom":[subQ2,subQ0]});Q43=makeQuery(id+"F3.imprint","IMPRINT",FACE,{"disambiguationData":[TD([[makeQuery(id+"F3.imprint","IMPRINT",EDGE,{"disambiguationData":[TD([[subQ3,-1.0]])],"derivedFrom":subQ2}),1.0]])]});}
            var Q44;
            {var subQ12=sQuery(id+"F3.wireOp",EDGE,"E41.0");var subQ13=sQuery(id+"F3.wireOp",EDGE,"E34");var subQ14=makeQuery(id+"F3.imprint","INTERSECT",VERTEX,{"derivedFrom":[subQ13,subQ12]});Q44=makeQuery(id+"F3.imprint","IMPRINT",FACE,{"disambiguationData":[TD([[makeQuery(id+"F3.imprint","IMPRINT",EDGE,{"disambiguationData":[TD([[subQ14,-1.0]])],"derivedFrom":subQ13}),-1.0]])]});}
            var Q45;
            {var subQ10=sQuery(id+"F3.wireOp",EDGE,"E41.0");var subQ11=sQuery(id+"F3.wireOp",EDGE,"E34");var subQ12=makeQuery(id+"F3.imprint","INTERSECT",VERTEX,{"derivedFrom":[subQ11,subQ10]});Q45=makeQuery(id+"F3.imprint","IMPRINT",FACE,{"disambiguationData":[TD([[makeQuery(id+"F3.imprint","IMPRINT",EDGE,{"disambiguationData":[TD([[subQ12,-1.0]])],"derivedFrom":subQ11}),1.0]])]});}
            var Q46;
            {var subQ0=sQuery(id+"F3.wireOp",EDGE,"E43.0");var subQ1=sQuery(id+"F0.wireOp",EDGE,"E4.5");var subQ2=makeQuery(id+"F1.opExtrude","CAP_EDGE",EDGE,{"disambiguationData":[OSD([subQ1])],"isStart":false});var subQ3=makeQuery(id+"F3.imprint","INTERSECT",VERTEX,{"derivedFrom":[subQ2,subQ0]});Q46=makeQuery(id+"F3.imprint","IMPRINT",FACE,{"disambiguationData":[TD([[makeQuery(id+"F3.imprint","IMPRINT",EDGE,{"disambiguationData":[TD([[subQ3,-1.0]])],"derivedFrom":subQ2}),1.0]])]});}
            var Q47;
            {var subQ0=sQuery(id+"F3.wireOp",EDGE,"E45.0");var subQ1=sQuery(id+"F0.wireOp",EDGE,"E4.5");var subQ2=makeQuery(id+"F1.opExtrude","CAP_EDGE",EDGE,{"disambiguationData":[OSD([subQ1])],"isStart":false});var subQ3=makeQuery(id+"F3.imprint","INTERSECT",VERTEX,{"derivedFrom":[subQ2,subQ0]});Q47=makeQuery(id+"F3.imprint","IMPRINT",FACE,{"disambiguationData":[TD([[makeQuery(id+"F3.imprint","IMPRINT",EDGE,{"disambiguationData":[TD([[subQ3,-1.0]])],"derivedFrom":subQ2}),1.0]])]});}
            var Q48;
            {var subQ2=sQuery(id+"F0.wireOp",EDGE,"E4.0");var subQ7=sQuery(id+"F3.wireOp",EDGE,"E47.0");var subQ11=makeQuery(id+"F1.opExtrude","CAP_EDGE",EDGE,{"disambiguationData":[OSD([subQ2])],"isStart":false});var subQ13=makeQuery(id+"F3.imprint","INTERSECT",VERTEX,{"derivedFrom":[subQ11,subQ7]});Q48=makeQuery(id+"F3.imprint","IMPRINT",FACE,{"disambiguationData":[TD([[makeQuery(id+"F3.imprint","IMPRINT",EDGE,{"disambiguationData":[TD([[subQ13,-1.0]])],"derivedFrom":subQ11}),1.0]])]});}
            var Q49;
            {var subQ11=sQuery(id+"F3.wireOp",EDGE,"E51.0");var subQ13=sQuery(id+"F3.wireOp",EDGE,"E34");var subQ14=makeQuery(id+"F3.imprint","INTERSECT",VERTEX,{"derivedFrom":[subQ13,subQ11]});Q49=makeQuery(id+"F3.imprint","IMPRINT",FACE,{"disambiguationData":[TD([[makeQuery(id+"F3.imprint","IMPRINT",EDGE,{"disambiguationData":[TD([[subQ14,-1.0]])],"derivedFrom":subQ13}),1.0]])]});}
            var Q50;
            {var subQ10=sQuery(id+"F3.wireOp",EDGE,"E50.0");var subQ11=sQuery(id+"F3.wireOp",EDGE,"E34");var subQ12=makeQuery(id+"F3.imprint","INTERSECT",VERTEX,{"derivedFrom":[subQ11,subQ10]});Q50=makeQuery(id+"F3.imprint","IMPRINT",FACE,{"disambiguationData":[TD([[makeQuery(id+"F3.imprint","IMPRINT",EDGE,{"disambiguationData":[TD([[subQ12,1.0]])],"derivedFrom":subQ11}),1.0]])]});}
            var Q51;
            {var subQ9=sQuery(id+"F3.wireOp",EDGE,"E51.0");var subQ10=sQuery(id+"F3.wireOp",EDGE,"E34");var subQ11=makeQuery(id+"F3.imprint","INTERSECT",VERTEX,{"derivedFrom":[subQ10,subQ9]});Q51=makeQuery(id+"F3.imprint","IMPRINT",FACE,{"disambiguationData":[TD([[makeQuery(id+"F3.imprint","IMPRINT",EDGE,{"disambiguationData":[TD([[subQ11,-1.0]])],"derivedFrom":subQ10}),-1.0]])]});}
            var Q52;
            {var subQ5=sQuery(id+"F3.wireOp",EDGE,"E34");var subQ7=sQuery(id+"F3.wireOp",EDGE,"E50.0");var subQ8=makeQuery(id+"F3.imprint","INTERSECT",VERTEX,{"derivedFrom":[subQ5,subQ7]});Q52=makeQuery(id+"F3.imprint","IMPRINT",FACE,{"disambiguationData":[TD([[makeQuery(id+"F3.imprint","IMPRINT",EDGE,{"disambiguationData":[TD([[subQ8,1.0]])],"derivedFrom":subQ5}),-1.0]])]});}
            var Q53;
            {var subQ0=sQuery(id+"F3.wireOp",EDGE,"E43.0");var subQ2=sQuery(id+"F0.wireOp",EDGE,"E4.3");var subQ5=makeQuery(id+"F1.opExtrude","CAP_EDGE",EDGE,{"disambiguationData":[OSD([subQ2])],"isStart":false});var subQ6=makeQuery(id+"F3.imprint","INTERSECT",VERTEX,{"derivedFrom":[subQ5,subQ0]});Q53=makeQuery(id+"F3.imprint","IMPRINT",FACE,{"disambiguationData":[TD([[makeQuery(id+"F3.imprint","IMPRINT",EDGE,{"disambiguationData":[TD([[subQ6,1.0]])],"derivedFrom":subQ5}),1.0]])]});}
            var Q54;
            {var subQ0=sQuery(id+"F3.wireOp",EDGE,"E45.0");var subQ2=sQuery(id+"F0.wireOp",EDGE,"E4.3");var subQ5=makeQuery(id+"F1.opExtrude","CAP_EDGE",EDGE,{"disambiguationData":[OSD([subQ2])],"isStart":false});var subQ6=makeQuery(id+"F3.imprint","INTERSECT",VERTEX,{"derivedFrom":[subQ5,subQ0]});Q54=makeQuery(id+"F3.imprint","IMPRINT",FACE,{"disambiguationData":[TD([[makeQuery(id+"F3.imprint","IMPRINT",EDGE,{"disambiguationData":[TD([[subQ6,1.0]])],"derivedFrom":subQ5}),1.0]])]});}
            var Q55;
            {var subQ0=sQuery(id+"F3.wireOp",EDGE,"E47.0");var subQ2=sQuery(id+"F0.wireOp",EDGE,"E4.2");var subQ5=makeQuery(id+"F1.opExtrude","CAP_EDGE",EDGE,{"disambiguationData":[OSD([subQ2])],"isStart":false});var subQ6=makeQuery(id+"F3.imprint","INTERSECT",VERTEX,{"derivedFrom":[subQ5,subQ0]});Q55=makeQuery(id+"F3.imprint","IMPRINT",FACE,{"disambiguationData":[TD([[makeQuery(id+"F3.imprint","IMPRINT",EDGE,{"disambiguationData":[TD([[subQ6,1.0]])],"derivedFrom":subQ5}),1.0]])]});}
            extrude(context, id + "F4", {"entities" : qUnion([Q0, Q1, Q2, Q3, Q4, Q5, Q6, Q7, Q8, Q9, Q10, Q11, Q12, Q13, Q14, Q15, Q16, Q17, Q18, Q19, Q20, Q21, Q22, Q23, Q24, Q25, Q26, Q27, Q28, Q29, Q30, Q31, Q32, Q33, Q34, Q35, Q36, Q37, Q38, Q39, Q40, Q41, Q42, Q43, Q44, Q45, Q46, Q47, Q48, Q49, Q50, Q51, Q52, Q53, Q54, Q55]), "operationType" : NewBodyOperationType.ADD, "depth" : 0.3 * mm, "offsetDistance" : 25 * mm, "hasSecondDirection" : true, "secondDirectionOppositeDirection" : true, "secondDirectionDepth" : 7.3 * mm});
        }
        {
            var Q0;
            Q0=makeQuery(id+"F0.imprint","IMPRINT",FACE,{"disambiguationData":[TD([[makeQuery(id+"F0.imprint","IMPRINT",EDGE,{"derivedFrom":sQuery(id+"F0.wireOp",EDGE,"E33")}),1.0]])]});
            extrude(context, id + "F5", {"entities" : qUnion([Q0]), "depth" : 1 * mm, "offsetDistance" : 25 * mm});
        }
        {
            var Q0;
            Q0=makeQuery(id+"F5.opExtrude","CAP_FACE",FACE,{"disambiguationData":[OSD([sQuery(id+"F0.wireOp",EDGE,"E33")])],"isStart":false});
            var sketch = newSketch(context, id + "F6", { "sketchPlane" : qUnion([Q0])});
            skCircle(sketch, "E53", {"center": v(-66.5, 53.35) * mm, "radius": 2.2 * mm});
            skCircle(sketch, "E54", {"center": v(-66.5, 53.35) * mm, "radius": 4.4 * mm});
            skCircle(sketch, "E55", {"center": v(-66.5, 53.35) * mm, "radius": 6.6 * mm});
            skCircle(sketch, "E56", {"center": v(-66.5, 53.35) * mm, "radius": 8.8 * mm});
            skSolve(sketch);
        }
        {
            var Q0;
            Q0=makeQuery(id+"F6.imprint","IMPRINT",FACE,{"disambiguationData":[TD([[makeQuery(id+"F6.imprint","IMPRINT",EDGE,{"derivedFrom":sQuery(id+"F6.wireOp",EDGE,"E55")}),-1.0]])]});
            var Q1;
            Q1=makeQuery(id+"F6.imprint","IMPRINT",FACE,{"disambiguationData":[TD([[makeQuery(id+"F6.imprint","IMPRINT",EDGE,{"derivedFrom":sQuery(id+"F6.wireOp",EDGE,"E53")}),-1.0]])]});
            extrude(context, id + "F7", {"entities" : qUnion([Q0, Q1]), "operationType" : NewBodyOperationType.ADD, "oppositeDirection" : true, "depth" : 1.3 * mm, "offsetDistance" : 25 * mm});
        }
        {
            var Q0;
            Q0=makeQuery(id+"F5.opExtrude","CAP_FACE",FACE,{"disambiguationData":[OSD([sQuery(id+"F0.wireOp",EDGE,"E33")])],"isStart":false});
            var sketch = newSketch(context, id + "F8", { "sketchPlane" : qUnion([Q0])});
            skCircle(sketch, "E57", {"center": v(-66.5, 53.35) * mm, "radius": 4 * mm});
            skSolve(sketch);
        }
        {
            var Q0;
            Q0=makeQuery(id+"F8.imprint","IMPRINT",FACE,{"disambiguationData":[TD([[makeQuery(id+"F8.imprint","IMPRINT",EDGE,{"derivedFrom":sQuery(id+"F8.wireOp",EDGE,"E57")}),1.0]])]});
            extrude(context, id + "F9", {"entities" : qUnion([Q0]), "operationType" : NewBodyOperationType.ADD, "depth" : 3 * mm, "offsetDistance" : 25 * mm});
        }
    });
